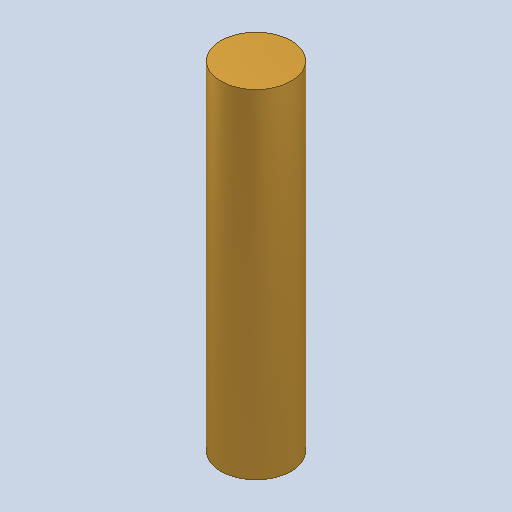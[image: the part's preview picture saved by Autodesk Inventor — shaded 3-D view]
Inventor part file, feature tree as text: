
AUTODESK INVENTOR PART (.ipt)
format: ipt  version: 2022.4 (Build 264492010, 492A)  size: 93,696 bytes
history: native  units: mm
features: other x1, sketch x1
ambient origin geometry x8: Origin, YZ Plane, XZ Plane, XY Plane, X Axis, Y Axis, Z Axis, Center Point
bodies: Solid2 (feature_tree), Solid1 (feature_tree)
feature tree (2):
  other  "Repaired Geometry1"
  sketch  "Sketch1"
